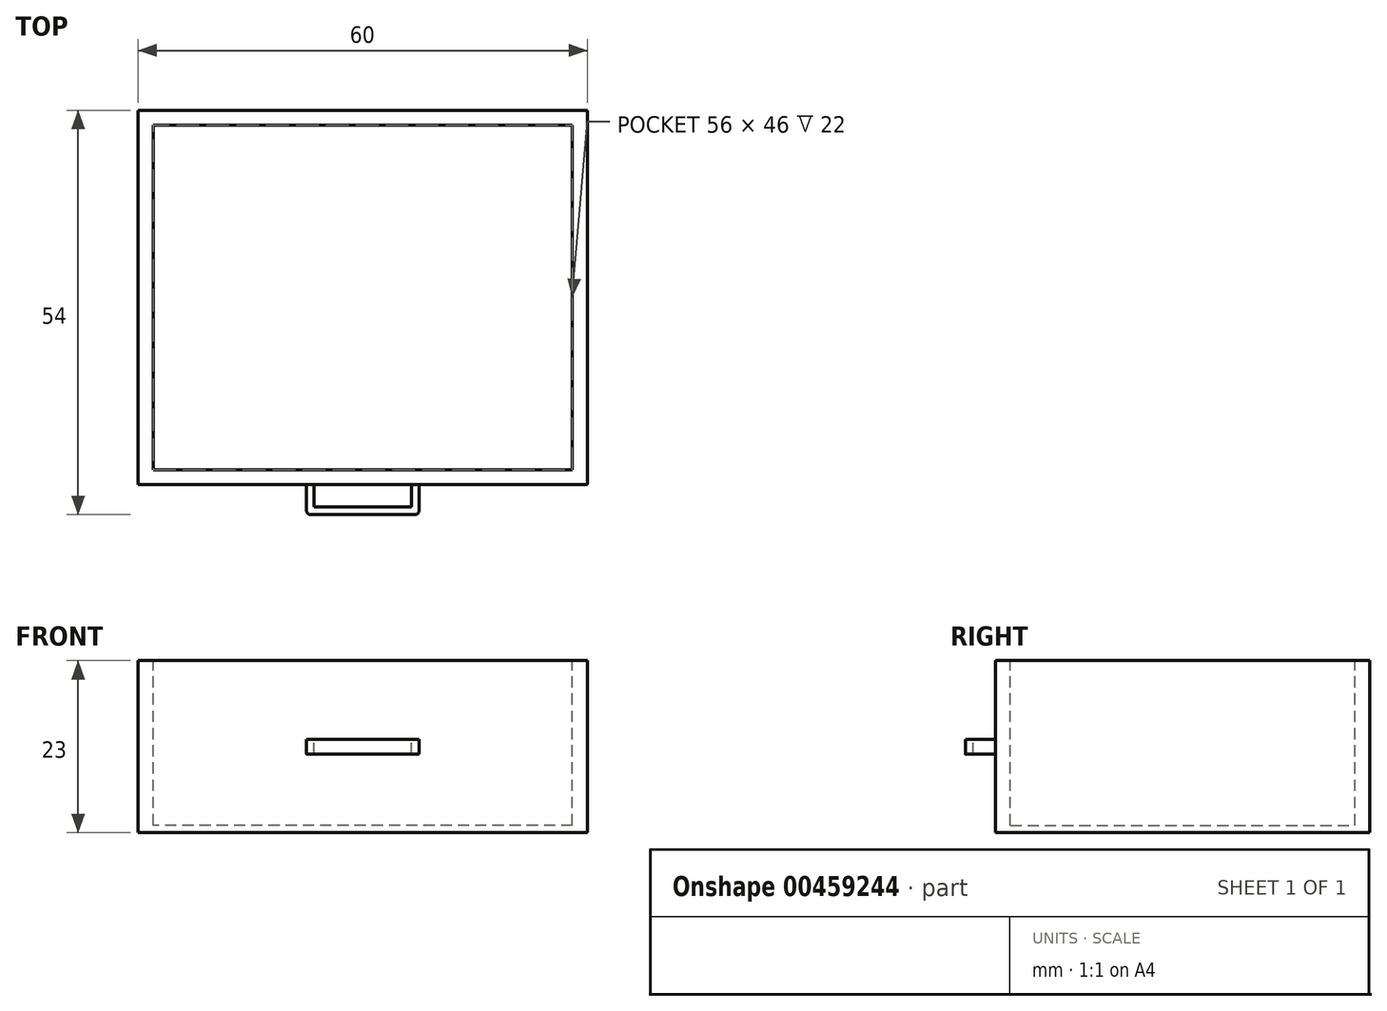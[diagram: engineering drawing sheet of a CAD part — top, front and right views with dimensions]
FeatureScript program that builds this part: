
annotation { "Feature Type Name" : "Feature", "Feature Type Description" : "" }
export const myFeature = defineFeature(function(context is Context, id is Id, definition is map)
    precondition{}
    {
        {
            var Q0;
            Q0=qCreatedBy(makeId("Front.planeOp"),FACE);
            var sketch = newSketch(context, id + "F0", { "sketchPlane" : qUnion([Q0])});
            skLineSegment(sketch, "E0.bottom", {"start": v(30, -11.5) * mm, "end": v(-30, -11.5) * mm});
            skLineSegment(sketch, "E0.top", {"start": v(30, 11.5) * mm, "end": v(-30, 11.5) * mm});
            skLineSegment(sketch, "E0.left", {"start": v(30, -11.5) * mm, "end": v(30, 11.5) * mm});
            skLineSegment(sketch, "E0.right", {"start": v(-30, -11.5) * mm, "end": v(-30, 11.5) * mm});
            skPoint(sketch, "E0.middle", {"position": v(0, 0) * mm});
            skSolve(sketch);
        }
        {
            var Q0;
            Q0 = qSketchRegion(id + "F0", true);
            extrude(context, id + "F1", {"entities" : qUnion([Q0]), "endBound" : BoundingType.SYMMETRIC, "depth" : 50 * mm});
        }
        {
            var Q0;
            Q0=makeQuery(id+"F1.opExtrude","SWEPT_FACE",FACE,{"disambiguationData":[OSD([sQuery(id+"F0.wireOp",EDGE,"E0.top")])]});
            var sketch = newSketch(context, id + "F2", { "sketchPlane" : qUnion([Q0])});
            skLineSegment(sketch, "E1.0", {"start": v(-28, -23) * mm, "end": v(-28, 23) * mm});
            skLineSegment(sketch, "E1.1", {"start": v(28, -23) * mm, "end": v(-28, -23) * mm});
            skLineSegment(sketch, "E1.2", {"start": v(28, -23) * mm, "end": v(28, 23) * mm});
            skLineSegment(sketch, "E1.3", {"start": v(28, 23) * mm, "end": v(-28, 23) * mm});
            skSolve(sketch);
        }
        {
            var Q0;
            Q0=makeQuery(id+"F2.imprint","IMPRINT",FACE,{"disambiguationData":[TD([[makeQuery(id+"F2.imprint","IMPRINT",EDGE,{"derivedFrom":sQuery(id+"F2.wireOp",EDGE,"E1.0")}),-1.0]])]});
            extrude(context, id + "F3", {"entities" : qUnion([Q0]), "operationType" : NewBodyOperationType.REMOVE, "oppositeDirection" : true, "depth" : 22 * mm});
        }
        {
            var Q0;
            Q0=makeQuery(id+"F1.opExtrude","CAP_FACE",FACE,{"disambiguationData":[OSD([sQuery(id+"F0.wireOp",EDGE,"E0.bottom"),sQuery(id+"F0.wireOp",EDGE,"E0.top"),sQuery(id+"F0.wireOp",EDGE,"E0.left"),sQuery(id+"F0.wireOp",EDGE,"E0.right")])],"isStart":false});
            var sketch = newSketch(context, id + "F4", { "sketchPlane" : qUnion([Q0])});
            skLineSegment(sketch, "E2.bottom", {"start": v(7.5, -1) * mm, "end": v(-7.5, -1) * mm});
            skLineSegment(sketch, "E2.top", {"start": v(7.5, 1) * mm, "end": v(-7.5, 1) * mm});
            skLineSegment(sketch, "E2.left", {"start": v(7.5, -1) * mm, "end": v(7.5, 1) * mm});
            skLineSegment(sketch, "E2.right", {"start": v(-7.5, -1) * mm, "end": v(-7.5, 1) * mm});
            skPoint(sketch, "E2.middle", {"position": v(0, 0) * mm});
            skSolve(sketch);
        }
        {
            var Q0;
            Q0=makeQuery(id+"F4.imprint","IMPRINT",FACE,{"disambiguationData":[TD([[makeQuery(id+"F4.imprint","IMPRINT",EDGE,{"derivedFrom":sQuery(id+"F4.wireOp",EDGE,"E2.bottom")}),-1.0]])]});
            extrude(context, id + "F5", {"entities" : qUnion([Q0]), "operationType" : NewBodyOperationType.ADD, "depth" : 4 * mm});
        }
        {
            var Q0;
            Q0=makeQuery(id+"F5.opExtrude","SWEPT_FACE",FACE,{"disambiguationData":[OSD([sQuery(id+"F4.wireOp",EDGE,"E2.top")])]});
            var sketch = newSketch(context, id + "F6", { "sketchPlane" : qUnion([Q0])});
            skLineSegment(sketch, "E3.0", {"start": v(-6.5, -28) * mm, "end": v(-6.5, -25) * mm});
            skLineSegment(sketch, "E3.1", {"start": v(6.5, -28) * mm, "end": v(-6.5, -28) * mm});
            skLineSegment(sketch, "E3.2", {"start": v(6.5, -28) * mm, "end": v(6.5, -25) * mm});
            skLineSegment(sketch, "E4", {"start": v(-6.5, -25) * mm, "end": v(6.5, -25) * mm});
            skSolve(sketch);
        }
        {
            var Q0;
            Q0=makeQuery(id+"F6.imprint","IMPRINT",FACE,{"disambiguationData":[TD([[makeQuery(id+"F6.imprint","IMPRINT",EDGE,{"derivedFrom":sQuery(id+"F6.wireOp",EDGE,"E3.0")}),-1.0]])]});
            extrude(context, id + "F7", {"entities" : qUnion([Q0]), "operationType" : NewBodyOperationType.REMOVE, "oppositeDirection" : true, "depth" : 2 * mm});
        }
        {
            var Q0;
            Q0=makeQuery(id+"F5.opExtrude","CAP_EDGE",EDGE,{"disambiguationData":[OSD([sQuery(id+"F4.wireOp",EDGE,"E2.right")])],"isStart":false});
            var Q1;
            Q1=makeQuery(id+"F5.opExtrude","CAP_EDGE",EDGE,{"disambiguationData":[OSD([sQuery(id+"F4.wireOp",EDGE,"E2.left")])],"isStart":false});
            fillet(context, id + "F8", {"entities" : qUnion([Q0, Q1]), "radius" : 0.5 * mm, "tangentPropagation" : true, "allowEdgeOverflow" : false});
        }
    });
